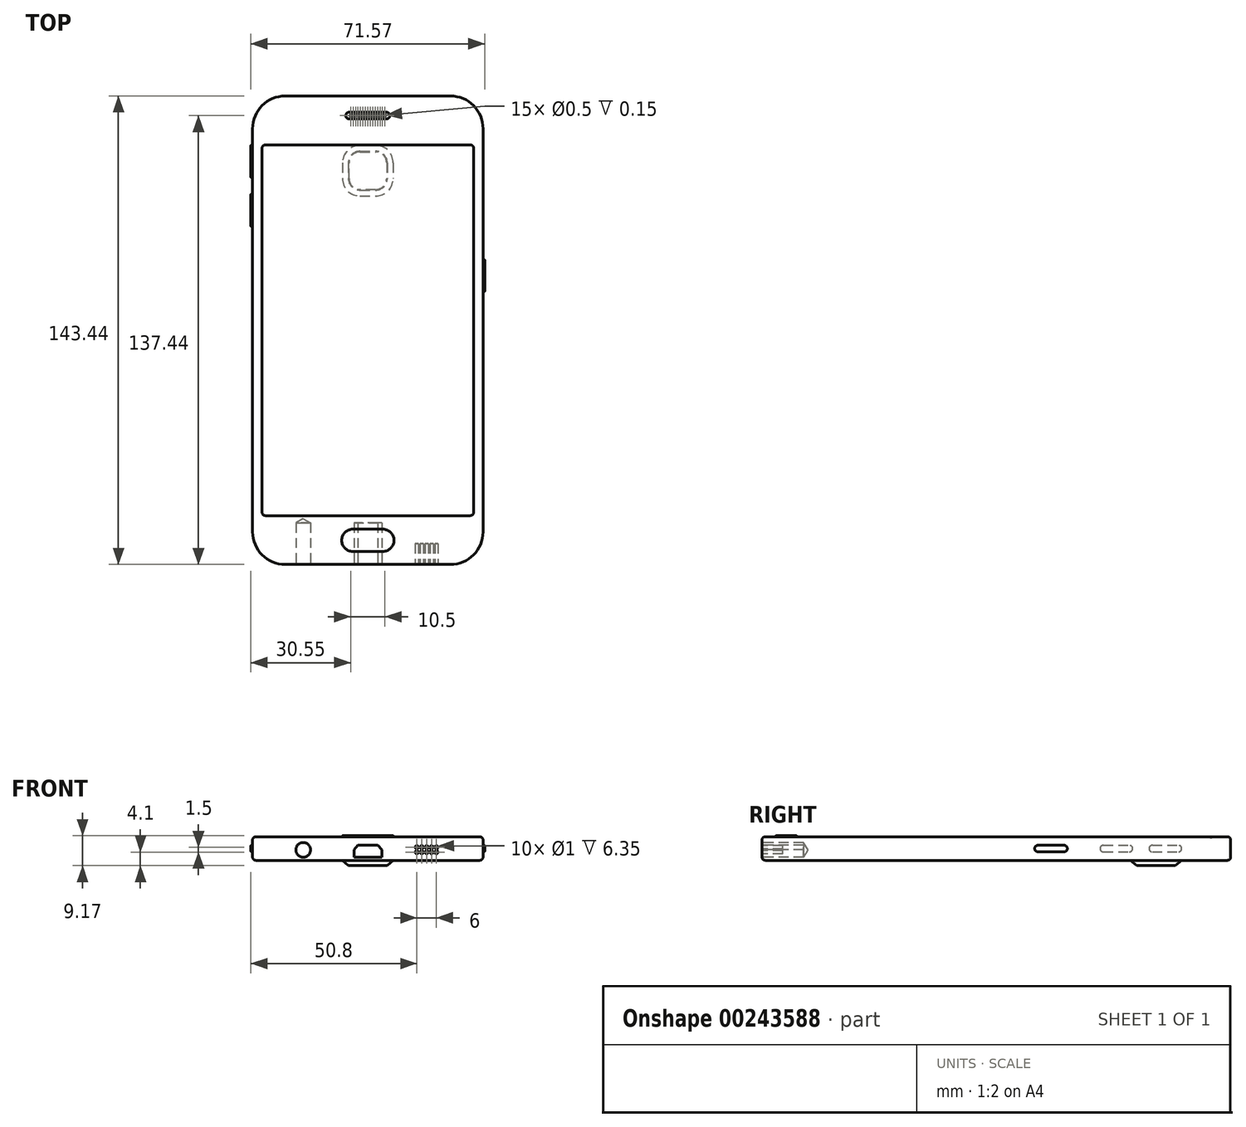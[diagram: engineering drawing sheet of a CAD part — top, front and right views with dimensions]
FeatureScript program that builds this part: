
annotation { "Feature Type Name" : "Feature", "Feature Type Description" : "" }
export const myFeature = defineFeature(function(context is Context, id is Id, definition is map)
    precondition{}
    {
        {
            var Q0;
            Q0=qCreatedBy(makeId("Top.planeOp"),FACE);
            var sketch = newSketch(context, id + "F0", { "sketchPlane" : qUnion([Q0])});
            skLineSegment(sketch, "E0.bottom", {"start": v(-35.27, 71.72) * mm, "end": v(35.27, 71.72) * mm});
            skLineSegment(sketch, "E0.top", {"start": v(-35.27, -71.72) * mm, "end": v(35.27, -71.72) * mm});
            skLineSegment(sketch, "E0.left", {"start": v(-35.27, 71.72) * mm, "end": v(-35.27, -71.72) * mm});
            skLineSegment(sketch, "E0.right", {"start": v(35.27, 71.72) * mm, "end": v(35.27, -71.72) * mm});
            skLineSegment(sketch, "E1", {"start": v(0, 0) * mm, "end": v(0, -71.72) * mm, "construction": true});
            skLineSegment(sketch, "E2", {"start": v(-35.27, 0) * mm, "end": v(0, 0) * mm, "construction": true});
            skPoint(sketch, "E3.orphan", {"position": v(35.27, 0) * mm});
            skPoint(sketch, "E4.orphan", {"position": v(0, 71.72) * mm});
            skSolve(sketch);
        }
        {
            var Q0;
            Q0=makeQuery(id+"F0.imprint","IMPRINT",FACE,{"disambiguationData":[TD([[makeQuery(id+"F0.imprint","IMPRINT",EDGE,{"derivedFrom":sQuery(id+"F0.wireOp",EDGE,"E0.bottom")}),-1.0]])]});
            extrude(context, id + "F1", {"entities" : qUnion([Q0]), "depth" : 7.22 * mm});
        }
        {
            var Q0;
            Q0=makeQuery(id+"F1.opExtrude","SWEPT_EDGE",EDGE,{"disambiguationData":[OSD([sQuery(id+"F0.wireOp",EDGE,"E0.bottom"),sQuery(id+"F0.wireOp",EDGE,"E0.left")])]});
            var Q1;
            Q1=makeQuery(id+"F1.opExtrude","SWEPT_EDGE",EDGE,{"disambiguationData":[OSD([sQuery(id+"F0.wireOp",EDGE,"E0.top"),sQuery(id+"F0.wireOp",EDGE,"E0.left")])]});
            var Q2;
            Q2=makeQuery(id+"F1.opExtrude","SWEPT_EDGE",EDGE,{"disambiguationData":[OSD([sQuery(id+"F0.wireOp",EDGE,"E0.top"),sQuery(id+"F0.wireOp",EDGE,"E0.right")])]});
            var Q3;
            Q3=makeQuery(id+"F1.opExtrude","SWEPT_EDGE",EDGE,{"disambiguationData":[OSD([sQuery(id+"F0.wireOp",EDGE,"E0.bottom"),sQuery(id+"F0.wireOp",EDGE,"E0.right")])]});
            fillet(context, id + "F2", {"entities" : qUnion([Q0, Q1, Q2, Q3]), "radius" : 10 * mm, "tangentPropagation" : true, "allowEdgeOverflow" : false});
        }
        {
            var Q0;
            Q0=makeQuery(id+"F1.opExtrude","CAP_FACE",FACE,{"disambiguationData":[OSD([sQuery(id+"F0.wireOp",EDGE,"E0.bottom"),sQuery(id+"F0.wireOp",EDGE,"E0.top"),sQuery(id+"F0.wireOp",EDGE,"E0.left"),sQuery(id+"F0.wireOp",EDGE,"E0.right")])],"isStart":false});
            var sketch = newSketch(context, id + "F3", { "sketchPlane" : qUnion([Q0])});
            skLineSegment(sketch, "E5.bottom", {"start": v(-4.6, -60.92) * mm, "end": v(4.6, -60.92) * mm});
            skLineSegment(sketch, "E5.top", {"start": v(-4.6, -67.72) * mm, "end": v(4.6, -67.72) * mm});
            skLineSegment(sketch, "E5.left", {"start": v(-8, -64.32) * mm, "end": v(-8, -64.32) * mm});
            skLineSegment(sketch, "E5.right", {"start": v(8, -64.32) * mm, "end": v(8, -64.32) * mm});
            skLineSegment(sketch, "E6", {"start": v(-8, -64.32) * mm, "end": v(8, -64.32) * mm, "construction": true});
            skLineSegment(sketch, "E7", {"start": v(0, -60.92) * mm, "end": v(0, -67.72) * mm, "construction": true});
            skPoint(sketch, "E8.visualSharp", {"position": v(-8, -60.92) * mm});
            skArc(sketch, "E8.filletArc", {"start": v(-4.6, -60.92) * mm, "mid": v(-7, -61.92) * mm, "end": v(-8, -64.32) * mm});
            skPoint(sketch, "E9.visualSharp", {"position": v(8, -60.92) * mm});
            skArc(sketch, "E9.filletArc", {"start": v(8, -64.32) * mm, "mid": v(7, -61.92) * mm, "end": v(4.6, -60.92) * mm});
            skPoint(sketch, "E10.visualSharp", {"position": v(8, -67.72) * mm});
            skArc(sketch, "E10.filletArc", {"start": v(4.6, -67.72) * mm, "mid": v(7, -66.72) * mm, "end": v(8, -64.32) * mm});
            skPoint(sketch, "E11.visualSharp", {"position": v(-8, -67.72) * mm});
            skArc(sketch, "E11.filletArc", {"start": v(-8, -64.32) * mm, "mid": v(-7, -66.72) * mm, "end": v(-4.6, -67.72) * mm});
            skSolve(sketch);
        }
        {
            var Q0;
            Q0=makeQuery(id+"F3.imprint","IMPRINT",FACE,{"disambiguationData":[TD([[makeQuery(id+"F3.imprint","IMPRINT",EDGE,{"derivedFrom":sQuery(id+"F3.wireOp",EDGE,"E5.bottom")}),-1.0]])]});
            extrude(context, id + "F4", {"entities" : qUnion([Q0]), "operationType" : NewBodyOperationType.ADD, "depth" : .35 * mm});
        }
        {
            var Q0;
            Q0=makeQuery(id+"F1.opExtrude","CAP_EDGE",EDGE,{"disambiguationData":[OSD([sQuery(id+"F0.wireOp",EDGE,"E0.left")])],"isStart":false});
            var Q1;
            Q1=makeQuery(id+"F1.opExtrude","CAP_EDGE",EDGE,{"disambiguationData":[OSD([sQuery(id+"F0.wireOp",EDGE,"E0.left")])],"isStart":true});
            fillet(context, id + "F5", {"entities" : qUnion([Q0, Q1]), "radius" : 1 * mm, "tangentPropagation" : true, "allowEdgeOverflow" : false});
        }
        {
            var Q0;
            Q0=makeQuery(id+"F1.opExtrude","SWEPT_FACE",FACE,{"disambiguationData":[OSD([sQuery(id+"F0.wireOp",EDGE,"E0.left")])]});
            var sketch = newSketch(context, id + "F6", { "sketchPlane" : qUnion([Q0])});
            skLineSegment(sketch, "E12.bottom", {"start": v(-31.72, 4.61) * mm, "end": v(-41.72, 4.61) * mm});
            skLineSegment(sketch, "E12.top", {"start": v(-31.72, 2.6) * mm, "end": v(-41.72, 2.61) * mm});
            skLineSegment(sketch, "E12.left", {"start": v(-31.72, 4.61) * mm, "end": v(-31.72, 2.6) * mm});
            skLineSegment(sketch, "E12.right", {"start": v(-41.72, 4.61) * mm, "end": v(-41.72, 2.61) * mm});
            skLineSegment(sketch, "E13.bottom", {"start": v(-46.72, 4.61) * mm, "end": v(-56.72, 4.61) * mm});
            skLineSegment(sketch, "E13.top", {"start": v(-46.72, 2.61) * mm, "end": v(-56.72, 2.61) * mm});
            skLineSegment(sketch, "E13.left", {"start": v(-46.72, 4.61) * mm, "end": v(-46.72, 2.61) * mm});
            skLineSegment(sketch, "E13.right", {"start": v(-56.72, 4.61) * mm, "end": v(-56.72, 2.61) * mm});
            skLineSegment(sketch, "E14", {"start": v(-31.72, 3.6) * mm, "end": v(-41.72, 3.6) * mm, "construction": true});
            skLineSegment(sketch, "E15", {"start": v(-36.72, 2.6) * mm, "end": v(-36.72, 4.6) * mm, "construction": true});
            skLineSegment(sketch, "E16", {"start": v(-51.72, 4.6) * mm, "end": v(-51.72, 2.61) * mm, "construction": true});
            skLineSegment(sketch, "E17", {"start": v(-46.72, 3.6) * mm, "end": v(-56.72, 3.6) * mm, "construction": true});
            skSolve(sketch);
        }
        {
            var Q0;
            Q0 = qSketchRegion(id + "F6", true);
            extrude(context, id + "F7", {"entities" : qUnion([Q0]), "operationType" : NewBodyOperationType.ADD, "depth" : .53 * mm});
        }
        {
            var Q0;
            Q0=makeQuery(id+"F7.opExtrude","SWEPT_EDGE",EDGE,{"disambiguationData":[OSD([sQuery(id+"F6.wireOp",EDGE,"E13.bottom"),sQuery(id+"F6.wireOp",EDGE,"E13.right")])]});
            var Q1;
            Q1=makeQuery(id+"F7.opExtrude","SWEPT_EDGE",EDGE,{"disambiguationData":[OSD([sQuery(id+"F6.wireOp",EDGE,"E13.top"),sQuery(id+"F6.wireOp",EDGE,"E13.right")])]});
            var Q2;
            Q2=makeQuery(id+"F7.opExtrude","SWEPT_EDGE",EDGE,{"disambiguationData":[OSD([sQuery(id+"F6.wireOp",EDGE,"E13.top"),sQuery(id+"F6.wireOp",EDGE,"E13.left")])]});
            var Q3;
            Q3=makeQuery(id+"F7.opExtrude","SWEPT_EDGE",EDGE,{"disambiguationData":[OSD([sQuery(id+"F6.wireOp",EDGE,"E13.bottom"),sQuery(id+"F6.wireOp",EDGE,"E13.left")])]});
            var Q4;
            Q4=makeQuery(id+"F7.opExtrude","SWEPT_EDGE",EDGE,{"disambiguationData":[OSD([sQuery(id+"F6.wireOp",EDGE,"E12.bottom"),sQuery(id+"F6.wireOp",EDGE,"E12.right")])]});
            var Q5;
            Q5=makeQuery(id+"F7.opExtrude","SWEPT_EDGE",EDGE,{"disambiguationData":[OSD([sQuery(id+"F6.wireOp",EDGE,"E12.top"),sQuery(id+"F6.wireOp",EDGE,"E12.right")])]});
            var Q6;
            Q6=makeQuery(id+"F7.opExtrude","SWEPT_EDGE",EDGE,{"disambiguationData":[OSD([sQuery(id+"F6.wireOp",EDGE,"E12.top"),sQuery(id+"F6.wireOp",EDGE,"E12.left")])]});
            var Q7;
            Q7=makeQuery(id+"F7.opExtrude","SWEPT_EDGE",EDGE,{"disambiguationData":[OSD([sQuery(id+"F6.wireOp",EDGE,"E12.bottom"),sQuery(id+"F6.wireOp",EDGE,"E12.left")])]});
            fillet(context, id + "F8", {"entities" : qUnion([Q0, Q1, Q2, Q3, Q4, Q5, Q6, Q7]), "radius" : 1 * mm, "tangentPropagation" : true, "allowEdgeOverflow" : false});
        }
        {
            var Q0;
            Q0=makeQuery(id+"F7.opExtrude","CAP_EDGE",EDGE,{"disambiguationData":[OSD([sQuery(id+"F6.wireOp",EDGE,"E13.top")])],"isStart":false});
            var Q1;
            Q1=makeQuery(id+"F7.opExtrude","CAP_EDGE",EDGE,{"disambiguationData":[OSD([sQuery(id+"F6.wireOp",EDGE,"E12.top")])],"isStart":false});
            fillet(context, id + "F9", {"entities" : qUnion([Q0, Q1]), "radius" : .25 * mm, "tangentPropagation" : true, "allowEdgeOverflow" : false});
        }
        {
            var Q0;
            Q0=makeQuery(id+"F1.opExtrude","CAP_FACE",FACE,{"disambiguationData":[OSD([sQuery(id+"F0.wireOp",EDGE,"E0.bottom"),sQuery(id+"F0.wireOp",EDGE,"E0.top"),sQuery(id+"F0.wireOp",EDGE,"E0.left"),sQuery(id+"F0.wireOp",EDGE,"E0.right")])],"isStart":true});
            var sketch = newSketch(context, id + "F10", { "sketchPlane" : qUnion([Q0])});
            skLineSegment(sketch, "E18.bottom", {"start": v(7.88, -40.97) * mm, "end": v(-7.87, -40.97) * mm});
            skLineSegment(sketch, "E18.top", {"start": v(7.88, -56.72) * mm, "end": v(-7.87, -56.72) * mm});
            skLineSegment(sketch, "E18.left", {"start": v(7.88, -40.97) * mm, "end": v(7.88, -56.72) * mm});
            skLineSegment(sketch, "E18.right", {"start": v(-7.87, -40.97) * mm, "end": v(-7.87, -56.72) * mm});
            skLineSegment(sketch, "E19", {"start": v(0, -40.97) * mm, "end": v(0, -56.72) * mm, "construction": true});
            skLineSegment(sketch, "E20", {"start": v(-7.87, -48.84) * mm, "end": v(7.88, -48.84) * mm, "construction": true});
            skSolve(sketch);
        }
        {
            var Q0;
            Q0 = qSketchRegion(id + "F10", true);
            extrude(context, id + "F11", {"entities" : qUnion([Q0]), "operationType" : NewBodyOperationType.ADD, "depth" : 1.6 * mm});
        }
        {
            var Q0;
            Q0=makeQuery(id+"F11.opExtrude","SWEPT_EDGE",EDGE,{"disambiguationData":[OSD([sQuery(id+"F10.wireOp",EDGE,"E18.bottom"),sQuery(id+"F10.wireOp",EDGE,"E18.right")])]});
            var Q1;
            Q1=makeQuery(id+"F11.opExtrude","SWEPT_EDGE",EDGE,{"disambiguationData":[OSD([sQuery(id+"F10.wireOp",EDGE,"E18.top"),sQuery(id+"F10.wireOp",EDGE,"E18.right")])]});
            var Q2;
            Q2=makeQuery(id+"F11.opExtrude","SWEPT_EDGE",EDGE,{"disambiguationData":[OSD([sQuery(id+"F10.wireOp",EDGE,"E18.top"),sQuery(id+"F10.wireOp",EDGE,"E18.left")])]});
            var Q3;
            Q3=makeQuery(id+"F11.opExtrude","SWEPT_EDGE",EDGE,{"disambiguationData":[OSD([sQuery(id+"F10.wireOp",EDGE,"E18.bottom"),sQuery(id+"F10.wireOp",EDGE,"E18.left")])]});
            fillet(context, id + "F12", {"entities" : qUnion([Q0, Q1, Q2, Q3]), "radius" : 5.5 * mm, "tangentPropagation" : true, "allowEdgeOverflow" : false});
        }
        {
            var Q0;
            Q0=makeQuery(id+"F11.opExtrude","CAP_EDGE",EDGE,{"disambiguationData":[OSD([sQuery(id+"F10.wireOp",EDGE,"E18.right")])],"isStart":false});
            chamfer(context, id + "F13", {"entities" : qUnion([Q0]), "chamferType" : ChamferType.OFFSET_ANGLE, "width" : 2 * mm, "oppositeDirection" : false, "angle" : 40 * degree, "tangentPropagation" : true});
        }
        {
            var Q0;
            {var subQ0=sQuery(id+"F10.wireOp",EDGE,"E18.right");var subQ1=sQuery(id+"F10.wireOp",EDGE,"E18.top");var subQ2=makeQuery(id+"F11.opExtrude","CAP_FACE",FACE,{"disambiguationData":[OSD([sQuery(id+"F10.wireOp",EDGE,"E18.bottom"),subQ1,sQuery(id+"F10.wireOp",EDGE,"E18.left"),subQ0])],"isStart":false});Q0=makeQuery(id+"F13.opChamfer","BLEND_EDGE",EDGE,{"blendedFrom":[makeQuery(id+"F12.opFillet","BLEND_EDGE",EDGE,{"blendedFrom":[makeQuery(id+"F11.opExtrude","SWEPT_EDGE",EDGE,{"disambiguationData":[OSD([subQ1,subQ0])]}),subQ2],"blendedInto":[subQ2]}),subQ2],"blendedInto":[subQ2]});}
            chamfer(context, id + "F14", {"entities" : qUnion([Q0]), "width" : .25 * mm, "tangentPropagation" : true});
        }
        {
            var Q0;
            Q0=makeQuery(id+"F4.opExtrude","CAP_EDGE",EDGE,{"disambiguationData":[OSD([sQuery(id+"F3.wireOp",EDGE,"E5.top")])],"isStart":false});
            fillet(context, id + "F15", {"entities" : qUnion([Q0]), "radius" : .5 * mm, "tangentPropagation" : true, "allowEdgeOverflow" : false});
        }
        {
            var Q0;
            Q0=makeQuery(id+"F1.opExtrude","SWEPT_FACE",FACE,{"disambiguationData":[OSD([sQuery(id+"F0.wireOp",EDGE,"E0.right")])]});
            var sketch = newSketch(context, id + "F16", { "sketchPlane" : qUnion([Q0])});
            skLineSegment(sketch, "E21.bottom", {"start": v(11.72, 4.61) * mm, "end": v(21.72, 4.61) * mm});
            skLineSegment(sketch, "E21.top", {"start": v(11.72, 2.61) * mm, "end": v(21.72, 2.61) * mm});
            skLineSegment(sketch, "E21.left", {"start": v(11.72, 4.61) * mm, "end": v(11.72, 2.61) * mm});
            skLineSegment(sketch, "E21.right", {"start": v(21.72, 4.61) * mm, "end": v(21.72, 2.61) * mm});
            skLineSegment(sketch, "E22", {"start": v(11.72, 3.6) * mm, "end": v(21.72, 3.6) * mm, "construction": true});
            skLineSegment(sketch, "E23", {"start": v(16.72, 2.61) * mm, "end": v(16.72, 4.61) * mm, "construction": true});
            skSolve(sketch);
        }
        {
            var Q0;
            Q0=makeQuery(id+"F16.imprint","IMPRINT",FACE,{"disambiguationData":[TD([[makeQuery(id+"F16.imprint","IMPRINT",EDGE,{"derivedFrom":sQuery(id+"F16.wireOp",EDGE,"E21.bottom")}),-1.0]])]});
            extrude(context, id + "F17", {"entities" : qUnion([Q0]), "operationType" : NewBodyOperationType.ADD, "depth" : .5 * mm});
        }
        {
            var Q0;
            Q0=makeQuery(id+"F17.opExtrude","SWEPT_EDGE",EDGE,{"disambiguationData":[OSD([sQuery(id+"F16.wireOp",EDGE,"E21.bottom"),sQuery(id+"F16.wireOp",EDGE,"E21.left")])]});
            var Q1;
            Q1=makeQuery(id+"F17.opExtrude","SWEPT_EDGE",EDGE,{"disambiguationData":[OSD([sQuery(id+"F16.wireOp",EDGE,"E21.top"),sQuery(id+"F16.wireOp",EDGE,"E21.left")])]});
            var Q2;
            Q2=makeQuery(id+"F17.opExtrude","SWEPT_EDGE",EDGE,{"disambiguationData":[OSD([sQuery(id+"F16.wireOp",EDGE,"E21.top"),sQuery(id+"F16.wireOp",EDGE,"E21.right")])]});
            var Q3;
            Q3=makeQuery(id+"F17.opExtrude","SWEPT_EDGE",EDGE,{"disambiguationData":[OSD([sQuery(id+"F16.wireOp",EDGE,"E21.bottom"),sQuery(id+"F16.wireOp",EDGE,"E21.right")])]});
            fillet(context, id + "F18", {"entities" : qUnion([Q0, Q1, Q2, Q3]), "radius" : 1 * mm, "tangentPropagation" : true, "allowEdgeOverflow" : false});
        }
        {
            var Q0;
            Q0=makeQuery(id+"F17.opExtrude","CAP_EDGE",EDGE,{"disambiguationData":[OSD([sQuery(id+"F16.wireOp",EDGE,"E21.bottom")])],"isStart":false});
            fillet(context, id + "F19", {"entities" : qUnion([Q0]), "radius" : .25 * mm, "tangentPropagation" : true, "allowEdgeOverflow" : false});
        }
        {
            var Q0;
            Q0=makeQuery(id+"F1.opExtrude","SWEPT_FACE",FACE,{"disambiguationData":[OSD([sQuery(id+"F0.wireOp",EDGE,"E0.top")])]});
            var sketch = newSketch(context, id + "F20", { "sketchPlane" : qUnion([Q0])});
            skCircle(sketch, "E24", {"center": v(-19.77, 3.2) * mm, "radius": 2.25 * mm});
            skSolve(sketch);
        }
        {
            var Q0;
            Q0=sQuery(id+"F20.wireOp",VERTEX,"E24.center");
            var Q1;
            Q1=makeQuery(id+"F1.opExtrude","SWEPT_BODY",BODY,{"disambiguationData":[OSD([sQuery(id+"F0.wireOp",EDGE,"E0.bottom"),sQuery(id+"F0.wireOp",EDGE,"E0.top"),sQuery(id+"F0.wireOp",EDGE,"E0.left"),sQuery(id+"F0.wireOp",EDGE,"E0.right")])]});
            hole(context, id + "F21", {"style" : HoleStyle.SIMPLE, "endStyle" : HoleEndStyle.BLIND, "holeDiameter" : 4.5 * mm, "holeDepth" : 12.7 * mm, "tappedDepth" : 12.7 * mm, "tapClearance" : 3, "locations" : qUnion([Q0]), "scope" : qUnion([Q1])});
        }
        {
            var Q0;
            Q0=makeQuery(id+"F1.opExtrude","SWEPT_FACE",FACE,{"disambiguationData":[OSD([sQuery(id+"F0.wireOp",EDGE,"E0.top")])]});
            var sketch = newSketch(context, id + "F22", { "sketchPlane" : qUnion([Q0])});
            skLineSegment(sketch, "E25", {"start": v(-4.25, 3.3) * mm, "end": v(-4.25, 1) * mm});
            skLineSegment(sketch, "E26", {"start": v(-4.25, 1) * mm, "end": v(4.25, 1) * mm});
            skLineSegment(sketch, "E27", {"start": v(4.25, 1) * mm, "end": v(4.25, 3.3) * mm});
            skLineSegment(sketch, "E28", {"start": v(4.25, 3.3) * mm, "end": v(3, 4.6) * mm});
            skLineSegment(sketch, "E29", {"start": v(3, 4.6) * mm, "end": v(-3, 4.6) * mm});
            skLineSegment(sketch, "E30", {"start": v(-3, 4.6) * mm, "end": v(-4.25, 3.3) * mm});
            skLineSegment(sketch, "E31", {"start": v(0, 4.6) * mm, "end": v(0, 1) * mm, "construction": true});
            skSolve(sketch);
        }
        {
            var Q0;
            Q0=makeQuery(id+"F22.imprint","IMPRINT",FACE,{"disambiguationData":[TD([[makeQuery(id+"F22.imprint","IMPRINT",EDGE,{"derivedFrom":sQuery(id+"F22.wireOp",EDGE,"E25")}),1.0]])]});
            extrude(context, id + "F23", {"entities" : qUnion([Q0]), "operationType" : NewBodyOperationType.REMOVE, "oppositeDirection" : true, "depth" : 12.7 * mm});
        }
        {
            var Q0;
            Q0=makeQuery(id+"F1.opExtrude","SWEPT_FACE",FACE,{"disambiguationData":[OSD([sQuery(id+"F0.wireOp",EDGE,"E0.top")])]});
            var sketch = newSketch(context, id + "F24", { "sketchPlane" : qUnion([Q0])});
            skCircle(sketch, "E32", {"center": v(15, 2.5) * mm, "radius": 0.5 * mm});
            skCircle(sketch, "E33.0.1.0", {"center": v(15, 4) * mm, "radius": 0.5 * mm});
            skCircle(sketch, "E33.1.0.0", {"center": v(16.5, 2.5) * mm, "radius": 0.5 * mm});
            skCircle(sketch, "E33.1.1.0", {"center": v(16.5, 4) * mm, "radius": 0.5 * mm});
            skCircle(sketch, "E33.2.0.0", {"center": v(18, 2.5) * mm, "radius": 0.5 * mm});
            skCircle(sketch, "E33.2.1.0", {"center": v(18, 4) * mm, "radius": 0.5 * mm});
            skCircle(sketch, "E33.3.0.0", {"center": v(19.5, 2.5) * mm, "radius": 0.5 * mm});
            skCircle(sketch, "E33.3.1.0", {"center": v(19.5, 4) * mm, "radius": 0.5 * mm});
            skCircle(sketch, "E33.4.0.0", {"center": v(21, 2.5) * mm, "radius": 0.5 * mm});
            skCircle(sketch, "E33.4.1.0", {"center": v(21, 4) * mm, "radius": 0.5 * mm});
            skLineSegment(sketch, "E33.direction1", {"start": v(15, 2.5) * mm, "end": v(16.5, 2.5) * mm, "construction": true});
            skLineSegment(sketch, "E33.direction2", {"start": v(15, 2.5) * mm, "end": v(15, 4) * mm, "construction": true});
            skSolve(sketch);
        }
        {
            var Q0;
            Q0 = qSketchRegion(id + "F24", true);
            extrude(context, id + "F25", {"entities" : qUnion([Q0]), "operationType" : NewBodyOperationType.REMOVE, "oppositeDirection" : true, "depth" : 6.35 * mm});
        }
        {
            var Q0;
            Q0=makeQuery(id+"F1.opExtrude","CAP_FACE",FACE,{"disambiguationData":[OSD([sQuery(id+"F0.wireOp",EDGE,"E0.bottom"),sQuery(id+"F0.wireOp",EDGE,"E0.top"),sQuery(id+"F0.wireOp",EDGE,"E0.left"),sQuery(id+"F0.wireOp",EDGE,"E0.right")])],"isStart":false});
            var sketch = newSketch(context, id + "F26", { "sketchPlane" : qUnion([Q0])});
            skCircle(sketch, "E34", {"center": v(-5.25, 65.72) * mm, "radius": 0.25 * mm});
            skCircle(sketch, "E35.1.0.0", {"center": v(-4.5, 65.72) * mm, "radius": 0.25 * mm});
            skCircle(sketch, "E35.2.0.0", {"center": v(-3.75, 65.72) * mm, "radius": 0.25 * mm});
            skCircle(sketch, "E35.3.0.0", {"center": v(-3, 65.72) * mm, "radius": 0.25 * mm});
            skCircle(sketch, "E35.4.0.0", {"center": v(-2.25, 65.72) * mm, "radius": 0.25 * mm});
            skCircle(sketch, "E35.5.0.0", {"center": v(-1.5, 65.72) * mm, "radius": 0.25 * mm});
            skCircle(sketch, "E35.6.0.0", {"center": v(-0.75, 65.72) * mm, "radius": 0.25 * mm});
            skCircle(sketch, "E35.7.0.0", {"center": v(0, 65.72) * mm, "radius": 0.25 * mm});
            skCircle(sketch, "E35.8.0.0", {"center": v(0.75, 65.72) * mm, "radius": 0.25 * mm});
            skCircle(sketch, "E35.9.0.0", {"center": v(1.5, 65.72) * mm, "radius": 0.25 * mm});
            skCircle(sketch, "E35.10.0.0", {"center": v(2.25, 65.72) * mm, "radius": 0.25 * mm});
            skCircle(sketch, "E35.11.0.0", {"center": v(3, 65.72) * mm, "radius": 0.25 * mm});
            skCircle(sketch, "E35.12.0.0", {"center": v(3.75, 65.72) * mm, "radius": 0.25 * mm});
            skCircle(sketch, "E35.13.0.0", {"center": v(4.5, 65.72) * mm, "radius": 0.25 * mm});
            skCircle(sketch, "E35.14.0.0", {"center": v(5.25, 65.72) * mm, "radius": 0.25 * mm});
            skLineSegment(sketch, "E35.direction1", {"start": v(-5.25, 65.72) * mm, "end": v(-4.5, 65.72) * mm, "construction": true});
            skLineSegment(sketch, "E36", {"start": v(0, 65.72) * mm, "end": v(0, 65.97) * mm, "construction": true});
            skSolve(sketch);
        }
        {
            var Q0;
            Q0 = qSketchRegion(id + "F26", true);
            extrude(context, id + "F27", {"entities" : qUnion([Q0]), "operationType" : NewBodyOperationType.REMOVE, "oppositeDirection" : true, "depth" : .25 * mm});
        }
        {
            var Q0;
            Q0=makeQuery(id+"F1.opExtrude","CAP_FACE",FACE,{"disambiguationData":[OSD([sQuery(id+"F0.wireOp",EDGE,"E0.bottom"),sQuery(id+"F0.wireOp",EDGE,"E0.top"),sQuery(id+"F0.wireOp",EDGE,"E0.left"),sQuery(id+"F0.wireOp",EDGE,"E0.right")])],"isStart":false});
            var sketch = newSketch(context, id + "F28", { "sketchPlane" : qUnion([Q0])});
            skLineSegment(sketch, "E37.bottom", {"start": v(-6.75, 66.72) * mm, "end": v(6.75, 66.72) * mm});
            skLineSegment(sketch, "E37.top", {"start": v(-6.75, 64.72) * mm, "end": v(6.75, 64.72) * mm});
            skLineSegment(sketch, "E37.left", {"start": v(-6.75, 66.72) * mm, "end": v(-6.75, 64.72) * mm});
            skLineSegment(sketch, "E37.right", {"start": v(6.75, 66.72) * mm, "end": v(6.75, 64.72) * mm});
            skLineSegment(sketch, "E38", {"start": v(0, 64.72) * mm, "end": v(0, 66.72) * mm, "construction": true});
            skLineSegment(sketch, "E39", {"start": v(-6.75, 65.72) * mm, "end": v(6.75, 65.72) * mm, "construction": true});
            skLineSegment(sketch, "E40", {"start": v(0, 65.97) * mm, "end": v(0, 65.47) * mm, "construction": true});
            skLineSegment(sketch, "E41", {"start": v(0, 65.72) * mm, "end": v(0.25, 65.72) * mm, "construction": true});
            skSolve(sketch);
        }
        {
            var Q0;
            Q0 = qSketchRegion(id + "F28", true);
            extrude(context, id + "F29", {"entities" : qUnion([Q0]), "operationType" : NewBodyOperationType.REMOVE, "oppositeDirection" : true, "depth" : .1 * mm});
        }
        {
            var Q0;
            Q0=makeQuery(id+"F29.boolean.opBoolean","COPY",EDGE,{"derivedFrom":makeQuery(id+"F29.opExtrude","SWEPT_EDGE",EDGE,{"disambiguationData":[OSD([sQuery(id+"F28.wireOp",EDGE,"E37.bottom"),sQuery(id+"F28.wireOp",EDGE,"E37.left")])]})});
            var Q1;
            Q1=makeQuery(id+"F29.boolean.opBoolean","COPY",EDGE,{"derivedFrom":makeQuery(id+"F29.opExtrude","SWEPT_EDGE",EDGE,{"disambiguationData":[OSD([sQuery(id+"F28.wireOp",EDGE,"E37.top"),sQuery(id+"F28.wireOp",EDGE,"E37.left")])]})});
            var Q2;
            Q2=makeQuery(id+"F29.boolean.opBoolean","COPY",EDGE,{"derivedFrom":makeQuery(id+"F29.opExtrude","SWEPT_EDGE",EDGE,{"disambiguationData":[OSD([sQuery(id+"F28.wireOp",EDGE,"E37.bottom"),sQuery(id+"F28.wireOp",EDGE,"E37.right")])]})});
            var Q3;
            Q3=makeQuery(id+"F29.boolean.opBoolean","COPY",EDGE,{"derivedFrom":makeQuery(id+"F29.opExtrude","SWEPT_EDGE",EDGE,{"disambiguationData":[OSD([sQuery(id+"F28.wireOp",EDGE,"E37.top"),sQuery(id+"F28.wireOp",EDGE,"E37.right")])]})});
            fillet(context, id + "F30", {"entities" : qUnion([Q0, Q1, Q2, Q3]), "radius" : 1 * mm, "tangentPropagation" : true, "allowEdgeOverflow" : false});
        }
        {
            var Q0;
            Q0=makeQuery(id+"F1.opExtrude","CAP_FACE",FACE,{"disambiguationData":[OSD([sQuery(id+"F0.wireOp",EDGE,"E0.bottom"),sQuery(id+"F0.wireOp",EDGE,"E0.top"),sQuery(id+"F0.wireOp",EDGE,"E0.left"),sQuery(id+"F0.wireOp",EDGE,"E0.right")])],"isStart":false});
            var sketch = newSketch(context, id + "F31", { "sketchPlane" : qUnion([Q0])});
            skLineSegment(sketch, "E42.bottom", {"start": v(-31.38, 56.75) * mm, "end": v(31.37, 56.75) * mm});
            skLineSegment(sketch, "E42.top", {"start": v(-31.38, -56.75) * mm, "end": v(31.38, -56.75) * mm});
            skLineSegment(sketch, "E42.left", {"start": v(-32.38, 55.75) * mm, "end": v(-32.38, -55.75) * mm});
            skLineSegment(sketch, "E42.right", {"start": v(32.37, 55.75) * mm, "end": v(32.37, -55.75) * mm});
            skLineSegment(sketch, "E43", {"start": v(0, 56.75) * mm, "end": v(0, -56.75) * mm, "construction": true});
            skPoint(sketch, "E43.endSnap0", {"position": v(0, -60.92) * mm});
            skLineSegment(sketch, "E44", {"start": v(-32.38, 0) * mm, "end": v(32.38, 0) * mm, "construction": true});
            skPoint(sketch, "E44.endSnap0", {"position": v(32.38, 0) * mm});
            skPoint(sketch, "E45.visualSharp", {"position": v(-32.38, 56.75) * mm});
            skArc(sketch, "E45.filletArc", {"start": v(-31.38, 56.75) * mm, "mid": v(-32.08, 56.46) * mm, "end": v(-32.38, 55.75) * mm});
            skPoint(sketch, "E46.visualSharp", {"position": v(32.37, 56.75) * mm});
            skArc(sketch, "E46.filletArc", {"start": v(32.38, 55.75) * mm, "mid": v(32.08, 56.46) * mm, "end": v(31.37, 56.75) * mm});
            skPoint(sketch, "E47.visualSharp", {"position": v(32.38, -56.75) * mm});
            skArc(sketch, "E47.filletArc", {"start": v(31.38, -56.75) * mm, "mid": v(32.08, -56.46) * mm, "end": v(32.38, -55.75) * mm});
            skPoint(sketch, "E48.visualSharp", {"position": v(-32.38, -56.75) * mm});
            skArc(sketch, "E48.filletArc", {"start": v(-32.38, -55.75) * mm, "mid": v(-32.08, -56.46) * mm, "end": v(-31.38, -56.75) * mm});
            skSolve(sketch);
        }
        {
            var Q0;
            Q0=makeQuery(id+"F31.imprint","IMPRINT",FACE,{"disambiguationData":[TD([[makeQuery(id+"F31.imprint","IMPRINT",EDGE,{"derivedFrom":sQuery(id+"F31.wireOp",EDGE,"E42.bottom")}),-1.0]])]});
            extrude(context, id + "F32", {"entities" : qUnion([Q0]), "operationType" : NewBodyOperationType.REMOVE, "oppositeDirection" : true, "depth" : .1 * mm});
        }
    });
